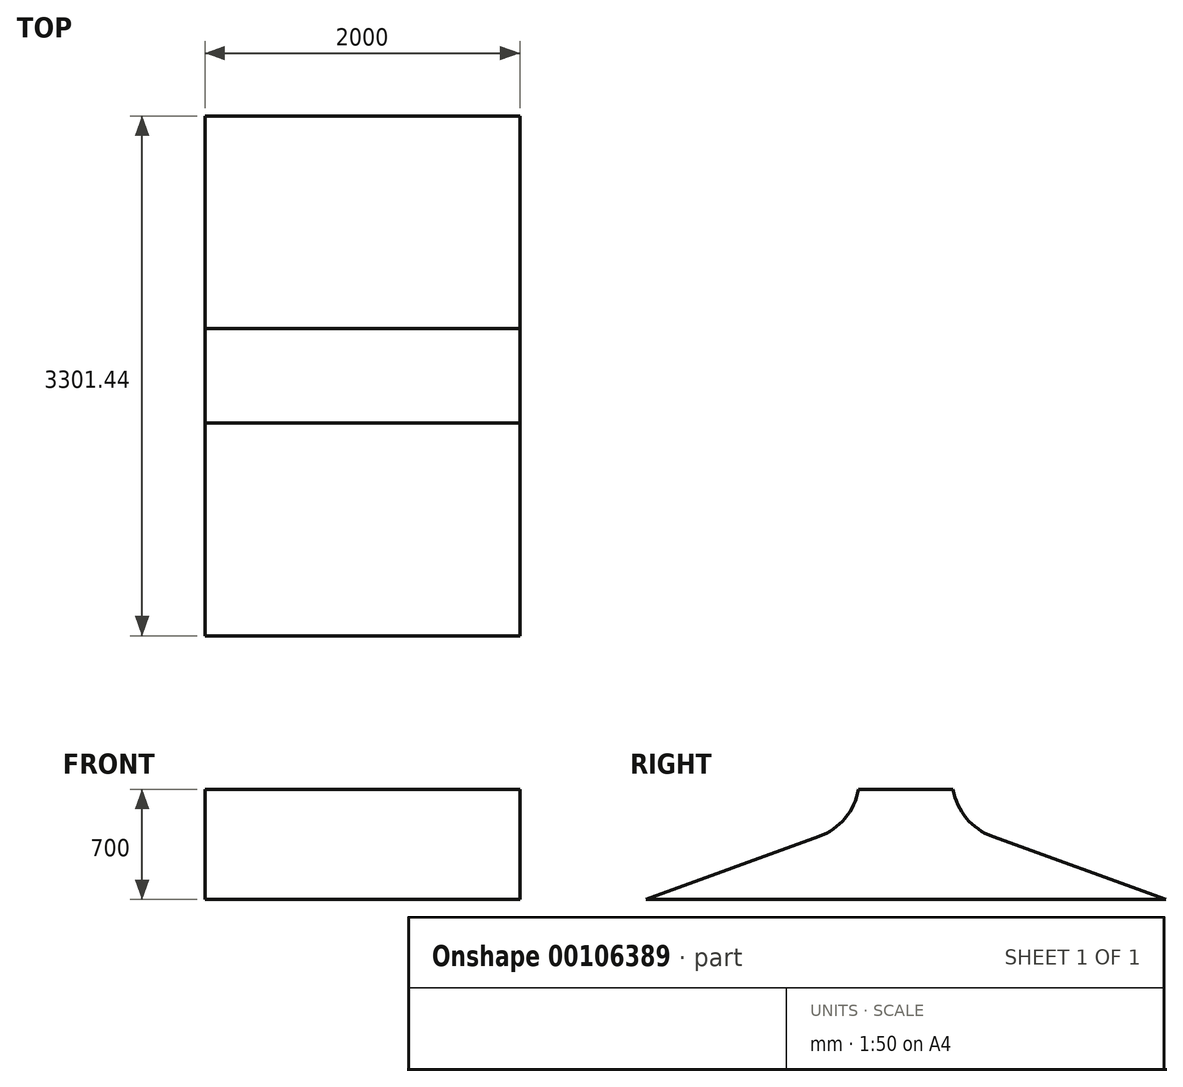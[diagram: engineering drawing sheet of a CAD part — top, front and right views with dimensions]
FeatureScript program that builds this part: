
annotation { "Feature Type Name" : "Feature", "Feature Type Description" : "" }
export const myFeature = defineFeature(function(context is Context, id is Id, definition is map)
    precondition{}
    {
        {
            var Q0;
            Q0=qCreatedBy(makeId("Right.planeOp"),FACE);
            var sketch = newSketch(context, id + "F0", { "sketchPlane" : qUnion([Q0])});
            skLineSegment(sketch, "E0", {"start": v(0, 0) * mm, "end": v(0, 700) * mm});
            skLineSegment(sketch, "E1", {"start": v(0, 700) * mm, "end": v(300, 700) * mm});
            skLineSegment(sketch, "E2", {"start": v(0, 0) * mm, "end": v(1650.72, 0) * mm});
            skLineSegment(sketch, "E3", {"start": v(1650.72, 0) * mm, "end": v(551.73, 400) * mm});
            skArc(sketch, "E4", {"start": v(551.73, 400) * mm, "mid": v(385.67, 516.27) * mm, "end": v(300, 700) * mm});
            skLineSegment(sketch, "E5", {"start": v(300, 700) * mm, "end": v(205.75, 1234.53) * mm, "construction": true});
            skSolve(sketch);
        }
        {
            var Q0;
            Q0=makeQuery(id+"F0.imprint","IMPRINT",FACE,{"disambiguationData":[TD([[makeQuery(id+"F0.imprint","IMPRINT",EDGE,{"derivedFrom":sQuery(id+"F0.wireOp",EDGE,"E0")}),-1.0]])]});
            extrude(context, id + "F1", {"entities" : qUnion([Q0]), "depth" : 2000 * mm});
        }
        {
            var Q0;
            Q0=makeQuery(id+"F1.opExtrude","SWEPT_BODY",BODY,{"disambiguationData":[OSD([sQuery(id+"F0.wireOp",EDGE,"E0"),sQuery(id+"F0.wireOp",EDGE,"E1"),sQuery(id+"F0.wireOp",EDGE,"E2"),sQuery(id+"F0.wireOp",EDGE,"E3"),sQuery(id+"F0.wireOp",EDGE,"E4")])]});
            var Q1;
            Q1=makeQuery(id+"F1.opExtrude","SWEPT_FACE",FACE,{"disambiguationData":[OSD([sQuery(id+"F0.wireOp",EDGE,"E0")])]});
            mirror(context, id + "F2", {"operationType" : NewBodyOperationType.ADD, "entities" : qUnion([Q0]), "mirrorPlane" : qUnion([Q1])});
        }
    });
